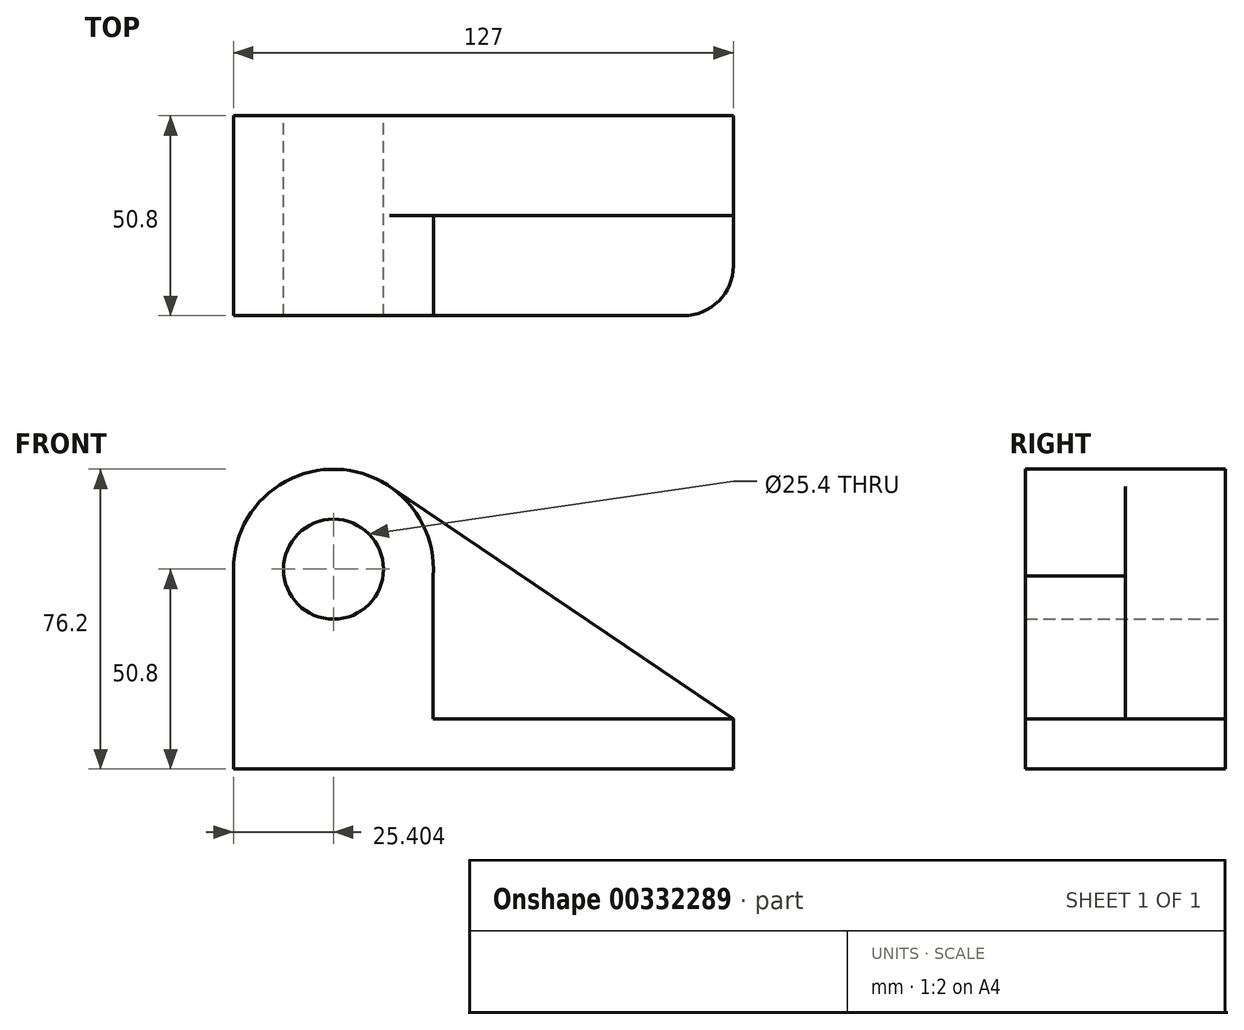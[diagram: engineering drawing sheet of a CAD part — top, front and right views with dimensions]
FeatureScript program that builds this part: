
annotation { "Feature Type Name" : "Feature", "Feature Type Description" : "" }
export const myFeature = defineFeature(function(context is Context, id is Id, definition is map)
    precondition{}
    {
        {
            var Q0;
            Q0=qCreatedBy(makeId("Front.planeOp"),FACE);
            var sketch = newSketch(context, id + "F0", { "sketchPlane" : qUnion([Q0])});
            skCircle(sketch, "E0", {"center": v(-45.5, 50.8) * mm, "radius": 12.7 * mm});
            skArc(sketch, "E1", {"start": v(-31.26, 71.83) * mm, "mid": v(-57.4, 73.24) * mm, "end": v(-70.9, 50.8) * mm});
            skLineSegment(sketch, "E2", {"start": v(-70.9, 50.8) * mm, "end": v(-70.9, 0) * mm});
            skLineSegment(sketch, "E3", {"start": v(-70.9, 0) * mm, "end": v(56.1, 0) * mm});
            skLineSegment(sketch, "E4", {"start": v(56.1, 0) * mm, "end": v(56.1, 12.7) * mm});
            skLineSegment(sketch, "E5", {"start": v(56.1, 12.7) * mm, "end": v(-31.26, 71.83) * mm});
            skSolve(sketch);
        }
        {
            var Q0;
            Q0 = qSketchRegion(id + "F0", true);
            extrude(context, id + "F1", {"entities" : qUnion([Q0]), "depth" : 25.4 * mm});
        }
        {
            var Q0;
            Q0=makeQuery(id+"F1.opExtrude","CAP_FACE",FACE,{"disambiguationData":[OSD([sQuery(id+"F0.wireOp",EDGE,"E0"),sQuery(id+"F0.wireOp",EDGE,"E1"),sQuery(id+"F0.wireOp",EDGE,"E2"),sQuery(id+"F0.wireOp",EDGE,"E3"),sQuery(id+"F0.wireOp",EDGE,"E4"),sQuery(id+"F0.wireOp",EDGE,"E5")])],"isStart":false});
            var sketch = newSketch(context, id + "F2", { "sketchPlane" : qUnion([Q0])});
            skCircle(sketch, "E6", {"center": v(-45.5, 50.8) * mm, "radius": 12.7 * mm});
            skArc(sketch, "E7", {"start": v(-20.16, 49.06) * mm, "mid": v(-44.62, 76.19) * mm, "end": v(-70.9, 50.8) * mm});
            skLineSegment(sketch, "E8.bottom", {"start": v(56.1, 12.7) * mm, "end": v(-20.16, 12.7) * mm});
            skLineSegment(sketch, "E8.left", {"start": v(56.1, 12.7) * mm, "end": v(56.1, 7.77) * mm});
            skLineSegment(sketch, "E8.right", {"start": v(-70.9, 12.7) * mm, "end": v(-70.9, 7.77) * mm});
            skLineSegment(sketch, "E9", {"start": v(-20.16, 49.06) * mm, "end": v(-20.16, 12.7) * mm});
            skSolve(sketch);
        }
        {
            var Q0;
            Q0=makeQuery(id+"F2.imprint","IMPRINT",FACE,{"disambiguationData":[TD([[makeQuery(id+"F2.imprint","IMPRINT",EDGE,{"derivedFrom":sQuery(id+"F2.wireOp",EDGE,"E6")}),-1.0]])]});
            extrude(context, id + "F3", {"entities" : qUnion([Q0]), "operationType" : NewBodyOperationType.ADD, "depth" : 25.4 * mm});
        }
        {
            var Q0;
            Q0=makeQuery(id+"F3.opExtrude","CAP_EDGE",EDGE,{"disambiguationData":[OSD([sQuery(id+"F0.wireOp",EDGE,"E4"),sQuery(id+"F2.wireOp",EDGE,"E8.left")])],"isStart":false});
            fillet(context, id + "F4", {"entities" : qUnion([Q0]), "radius" : 12.7 * mm, "tangentPropagation" : true, "allowEdgeOverflow" : false});
        }
    });
